# Revit family: О-ВО
name_source: partatom
category: Арматура воздуховодов
units: mm (PartAtom-declared; Revit-internal decimal feet)

## family parameters
Всегда вертикально = Да
На основе рабочей плоскости = Нет
Общий = Нет
При загрузке вырезать с полостями = Нет
Размер круглого соединителя = Использовать диаметр
Тип детали = Присоединяется

## types (11) — shared parameters
00_20_Manufacturer = Вентс
00_20_Name = Опора
Casing Material = Условный материал-отделка
Grid Material = Cover Grid Cross
Load Classification = HVAC
Maintenance zone material = <По категории>
d = 8 мм
n = 4
zero-valued in all types: Отметка по умолчанию

## per-type parameters (varying)
| type | A | A1 | B | B1 | H | M | M1 | R1 | R2 | R3 | R4 | a | Вес |
| О-ВО-400 | 510 мм | 500 мм | 395 мм | 385 мм | 115 мм | 45 мм | 40 мм | 207 мм | 225 мм | 289 мм | 64 мм | 160 мм | 1.15 кг |
| О-ВО-450 | 560 мм | 550 мм | 435 мм | 425 мм | 125 мм | 45 мм | 40 мм | 232 мм | 250 мм | 319 мм | 69 мм | 180 мм | 1.3 кг |
| О-ВО-500 | 610 мм | 600 мм | 480 мм | 470 мм | 130 мм | 45 мм | 40 мм | 257 мм | 280 мм | 352 мм | 72 мм | 200 мм | 1.4 кг |
| О-ВО-560 | 670 мм | 660 мм | 525 мм | 515 мм | 140 мм | 45 мм | 40 мм | 287 мм | 310 мм | 388 мм | 78 мм | 230 мм | 1.6 кг |
| О-ВО-630 | 740 мм | 730 мм | 575 мм | 565 мм | 150 мм | 45 мм | 40 мм | 322 мм | 345 мм | 428 мм | 83 мм | 255 мм | 1.8 кг |
| О-ВО-710 | 820 мм | 810 мм | 630 мм | 620 мм | 160 мм | 45 мм | 40 мм | 362 мм | 385 мм | 474 мм | 89 мм | 280 мм | 2 кг |
| О-ВО-800 | 910 мм | 900 мм | 705 мм | 695 мм | 180 мм | 45 мм | 40 мм | 407 мм | 430 мм | 530 мм | 100 мм | 315 мм | 2.35 кг |
| О-ВО-900 | 1020 мм | 1010 мм | 795 мм | 785 мм | 215 мм | 52 мм | 47 мм | 457 мм | 485 мм | 604 мм | 119 мм | 360 мм | 6.3 кг |
| О-ВО-1000 | 1120 мм | 1110 мм | 875 мм | 865 мм | 235 мм | 52 мм | 47 мм | 507 мм | 535 мм | 666 мм | 131 мм | 400 мм | 7.2 кг |
| О-ВО-1120 | 1240 мм | 1230 мм | 1002 мм | 992 мм | 270 мм | 52 мм | 47 мм | 567 мм | 595 мм | 745 мм | 150 мм | 460 мм | 9.1 кг |
| О-ВО-1250 | 1370 мм | 1360 мм | 1087 мм | 1077 мм | 285 мм | 52 мм | 47 мм | 632 мм | 660 мм | 818 мм | 158 мм | 510 мм | 10.25 кг |

note: column(s) folded — value = type name in every type: 00_20_Type
